# Revit family: HVAC_Air-Conditioning_Ice-Air_RSXC
name_source: partatom
category: Mechanical Equipment
units: mm (PartAtom-declared; Revit-internal decimal feet)

## family parameters
Classification = None
Cut with Voids When Loaded = No
Host = Face
OmniClass Number = 23.75.10.24.21.27.21
Part Type = Normal
Room Calculation Point = No
Round Connector Dimension = Use Diameter
Shared = No

## types (10) — shared parameters
Cooling Coil Connection Diameter = 1"
Default Elevation = 48 "
Description = RSXC Series Cold Climate Packaged Terminal Air Conditioner
Drain Pipe Diameter = 0.75 "
Evaporator Motor Nominal HP = 1/25
Frequency = 60 Hz
Height = 16.69 "
Length = 20.13 "
Manufacturer = Ice Air
Outside Air = 60 CFM
Phase = 1
Power Factor = 1
Product Material = Ice Air - Metal - Aluminium
Product Page URL = https://www.ice-air.com
URL = https://www.ice-air.com
Width = 41.81 "

## per-type parameters (varying)
- RSXC18-4.3kW: Airflow=480 CFM; COP=3.0; COP @ -5°F=1.6; COP @ 10°F=2.02; COP @ 5°F=1.93; Cooling Capacity Range=7,300 - 18,000; Current in Cooling Operation=8 A; Current in Heating Operation=8 A; Electric Heater=4300.00 W; Electric Heater (A)=21 A; Energy Efficiency Rating=10; HSPF=9.0; Heating Capacity @ -5°F=8,100; Heating Capacity @ 10°F=11,600; Heating Capacity @ 5°F=10,600; Heating Capacity Range=9,500 – 18,700; MCA (with Electric Heat)=26.4; MCA (without Electric Heat)=10.4; MOCP (with Electric Heat)=30; MOCP (without Electric Heat)=15; Power in Cooling Operation=1630.00 W; Power in Heating Operation=1690.00 W; Sensible Cooling Capacity=3282.4 W; Total Cooling Capacity=1630.0 W; Total Heating Capacity=1690.0 W; Voltage=208 V; Weight=151.00 lbf
- RSXC18-3.5kW: Airflow=480 CFM; COP=3.0; COP @ -5°F=1.6; COP @ 10°F=2.02; COP @ 5°F=1.93; Cooling Capacity Range=7,300 - 18,000; Current in Cooling Operation=8 A; Current in Heating Operation=8 A; Electric Heater=3500.00 W; Electric Heater (A)=17 A; Energy Efficiency Rating=10; HSPF=9.0; Heating Capacity @ -5°F=8,100; Heating Capacity @ 10°F=11,600; Heating Capacity @ 5°F=10,600; Heating Capacity Range=9,500 – 18,700; MCA (with Electric Heat)=21.5; MCA (without Electric Heat)=10.4; MOCP (with Electric Heat)=25; MOCP (without Electric Heat)=15; Power in Cooling Operation=1630.00 W; Power in Heating Operation=1690.00 W; Sensible Cooling Capacity=3282.4 W; Total Cooling Capacity=1630.0 W; Total Heating Capacity=1690.0 W; Voltage=208 V; Weight=151.00 lbf
- RSXC18-3.0kW: Airflow=480 CFM; COP=3.0; COP @ -5°F=1.6; COP @ 10°F=2.02; COP @ 5°F=1.93; Cooling Capacity Range=7,300 - 18,000; Current in Cooling Operation=8 A; Current in Heating Operation=8 A; Electric Heater=3000.00 W; Electric Heater (A)=14 A; Energy Efficiency Rating=10; HSPF=9.0; Heating Capacity @ -5°F=8,100; Heating Capacity @ 10°F=11,600; Heating Capacity @ 5°F=10,600; Heating Capacity Range=9,500 – 18,700; MCA (with Electric Heat)=18.4; MCA (without Electric Heat)=10.4; MOCP (with Electric Heat)=20; MOCP (without Electric Heat)=15; Power in Cooling Operation=1630.00 W; Power in Heating Operation=1690.00 W; Sensible Cooling Capacity=3282.4 W; Total Cooling Capacity=1630.0 W; Total Heating Capacity=1690.0 W; Voltage=208 V; Weight=151.00 lbf
- RSXC13-4.3kW: Airflow=400 CFM; COP=3.1; COP @ -5°F=1.62; COP @ 10°F=2.14; COP @ 5°F=1.91; Cooling Capacity Range=6,500 – 14,900; Current in Cooling Operation=5 A; Current in Heating Operation=6 A; Electric Heater=4300.00 W; Electric Heater (A)=21 A; Energy Efficiency Rating=11.1; HSPF=9.5; Heating Capacity @ -5°F=6,400; Heating Capacity @ 10°F=7,700; Heating Capacity @ 5°F=6,900; Heating Capacity Range=5,600 – 14,200; MCA (with Electric Heat)=26.4; MCA (without Electric Heat)=8.5; MOCP (with Electric Heat)=30; MOCP (without Electric Heat)=15; Power in Cooling Operation=1126.00 W; Power in Heating Operation=1134.00 W; Sensible Cooling Capacity=2579.0 W; Total Cooling Capacity=1126.0 W; Total Heating Capacity=1134.0 W; Voltage=208 V; Weight=134.00 lbf
- RSXC13-3.5kW: Airflow=400 CFM; COP=3.1; COP @ -5°F=1.62; COP @ 10°F=2.14; COP @ 5°F=1.91; Cooling Capacity Range=6,500 – 14,900; Current in Cooling Operation=5 A; Current in Heating Operation=6 A; Electric Heater=3500.00 W; Electric Heater (A)=17 A; Energy Efficiency Rating=11.1; HSPF=9.5; Heating Capacity @ -5°F=6,400; Heating Capacity @ 10°F=7,700; Heating Capacity @ 5°F=6,900; Heating Capacity Range=5,600 – 14,200; MCA (with Electric Heat)=21.5; MCA (without Electric Heat)=8.5; MOCP (with Electric Heat)=25; MOCP (without Electric Heat)=15; Power in Cooling Operation=1126.00 W; Power in Heating Operation=1134.00 W; Sensible Cooling Capacity=2579.0 W; Total Cooling Capacity=1126.0 W; Total Heating Capacity=1134.0 W; Voltage=208 V; Weight=134.00 lbf
- RSXC13-3.0kW: Airflow=400 CFM; COP=3.1; COP @ -5°F=1.62; COP @ 10°F=2.14; COP @ 5°F=1.91; Cooling Capacity Range=6,500 – 14,900; Current in Cooling Operation=5 A; Current in Heating Operation=6 A; Electric Heater=3000.00 W; Electric Heater (A)=14 A; Energy Efficiency Rating=11.1; HSPF=9.5; Heating Capacity @ -5°F=6,400; Heating Capacity @ 10°F=7,700; Heating Capacity @ 5°F=6,900; Heating Capacity Range=5,600 – 14,200; MCA (with Electric Heat)=18.4; MCA (without Electric Heat)=8.5; MOCP (with Electric Heat)=20; MOCP (without Electric Heat)=15; Power in Cooling Operation=1126.00 W; Power in Heating Operation=1134.00 W; Sensible Cooling Capacity=2579.0 W; Total Cooling Capacity=1126.0 W; Total Heating Capacity=1134.0 W; Voltage=208 V; Weight=134.00 lbf
- RSXC13-1.5kW: Airflow=400 CFM; COP=3.1; COP @ -5°F=1.62; COP @ 10°F=2.14; COP @ 5°F=1.91; Cooling Capacity Range=6,500 – 14,900; Current in Cooling Operation=10 A; Current in Heating Operation=10 A; Electric Heater=1500.00 W; Electric Heater (A)=13 A; Energy Efficiency Rating=11.1; HSPF=9.5; Heating Capacity @ -5°F=6,400; Heating Capacity @ 10°F=7,700; Heating Capacity @ 5°F=6,900; Heating Capacity Range=5,600 – 14,200; MCA (with Electric Heat)=17.0; MCA (without Electric Heat)=12.6; MOCP (with Electric Heat)=20; MOCP (without Electric Heat)=20; Power in Cooling Operation=1126.00 W; Power in Heating Operation=1134.00 W; Sensible Cooling Capacity=2579.0 W; Total Cooling Capacity=1126.0 W; Total Heating Capacity=1134.0 W; Voltage=115 V; Weight=134.00 lbf
- RSXC09-3.5kW: Airflow=380 CFM; COP=3.6; COP @ -5°F=1.74; COP @ 10°F=2.2; COP @ 5°F=1.98; Cooling Capacity Range=6,300 – 11,800; Current in Cooling Operation=4 A; Current in Heating Operation=4 A; Electric Heater=3500.00 W; Electric Heater (A)=17 A; Energy Efficiency Rating=12.1; HSPF=9.6; Heating Capacity @ -5°F=5,500; Heating Capacity @ 10°F=6,600; Heating Capacity @ 5°F=6,100; Heating Capacity Range=5,200 – 12,600; MCA (with Electric Heat)=21.5; MCA (without Electric Heat)=5.9; MOCP (with Electric Heat)=25; MOCP (without Electric Heat)=15; Power in Cooling Operation=760.00 W; Power in Heating Operation=830.00 W; Sensible Cooling Capacity=2110.1 W; Total Cooling Capacity=760.0 W; Total Heating Capacity=830.0 W; Voltage=208 V; Weight=127.00 lbf
- RSXC09-3.0kW: Airflow=380 CFM; COP=3.6; COP @ -5°F=1.74; COP @ 10°F=2.2; COP @ 5°F=1.98; Cooling Capacity Range=6,300 – 11,800; Current in Cooling Operation=4 A; Current in Heating Operation=4 A; Electric Heater=3000.00 W; Electric Heater (A)=14 A; Energy Efficiency Rating=12.1; HSPF=9.6; Heating Capacity @ -5°F=5,500; Heating Capacity @ 10°F=6,600; Heating Capacity @ 5°F=6,100; Heating Capacity Range=5,200 – 12,600; MCA (with Electric Heat)=18.4; MCA (without Electric Heat)=5.9; MOCP (with Electric Heat)=20; MOCP (without Electric Heat)=15; Power in Cooling Operation=760.00 W; Power in Heating Operation=830.00 W; Sensible Cooling Capacity=2110.1 W; Total Cooling Capacity=760.0 W; Total Heating Capacity=830.0 W; Voltage=208 V; Weight=127.00 lbf
- RSXC09-1.5kW: Airflow=380 CFM; COP=3.6; COP @ -5°F=1.74; COP @ 10°F=2.2; COP @ 5°F=1.98; Cooling Capacity Range=6,300 – 11,800; Current in Cooling Operation=7 A; Current in Heating Operation=7 A; Electric Heater=1500.00 W; Electric Heater (A)=13 A; Energy Efficiency Rating=12.1; HSPF=9.6; Heating Capacity @ -5°F=5,500; Heating Capacity @ 10°F=6,600; Heating Capacity @ 5°F=6,100; Heating Capacity Range=5,200 – 12,600; MCA (with Electric Heat)=17.0; MCA (without Electric Heat)=11.7; MOCP (with Electric Heat)=20; MOCP (without Electric Heat)=20; Power in Cooling Operation=760.00 W; Power in Heating Operation=830.00 W; Sensible Cooling Capacity=2110.1 W; Total Cooling Capacity=760.0 W; Total Heating Capacity=830.0 W; Voltage=115 V; Weight=127.00 lbf

note: column(s) folded — value = type name in every type: Model

## geometry (parser evidence)
native form markers: Sweep x2
no freeform markers — native parametric forms only
